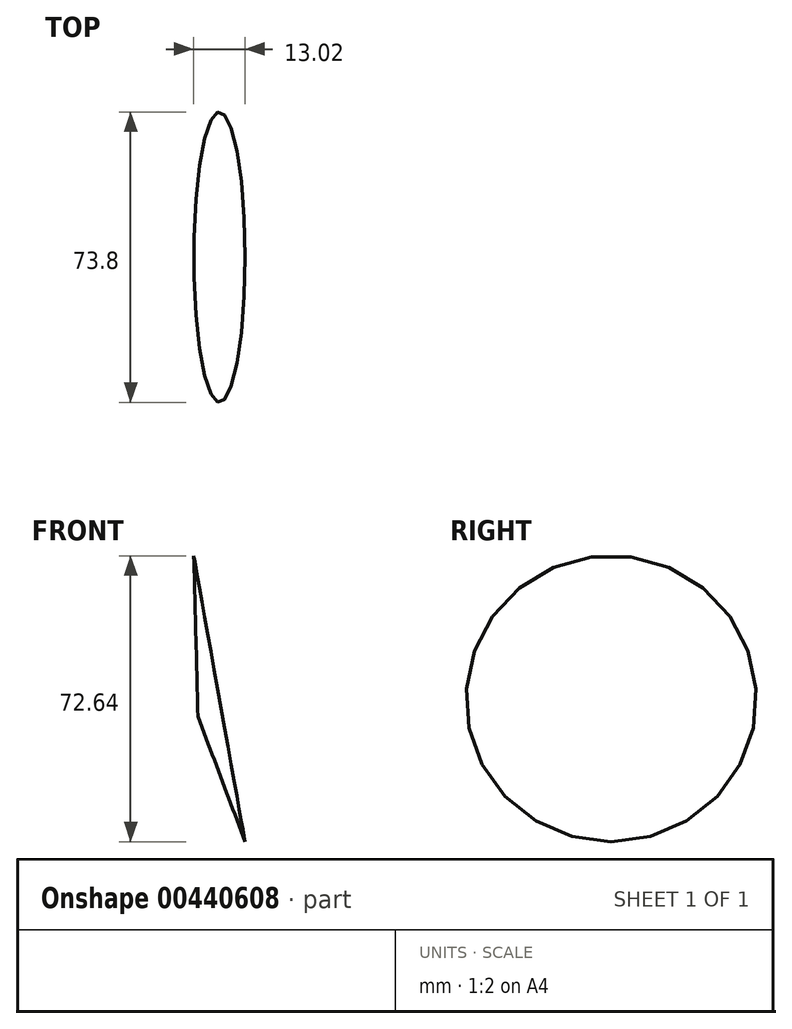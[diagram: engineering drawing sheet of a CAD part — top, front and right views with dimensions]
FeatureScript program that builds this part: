
annotation { "Feature Type Name" : "Feature", "Feature Type Description" : "" }
export const myFeature = defineFeature(function(context is Context, id is Id, definition is map)
    precondition{}
    {
        {
            var Q0;
            Q0=qCreatedBy(makeId("Front.planeOp"),FACE);
            var sketch = newSketch(context, id + "F0", { "sketchPlane" : qUnion([Q0])});
            skLineSegment(sketch, "E0", {"start": v(2.62, -61.14) * mm, "end": v(13.02, -91.95) * mm});
            skPoint(sketch, "E1.visualSharp", {"position": v(0, -53.36) * mm});
            skArc(sketch, "E1.filletArc", {"start": v(0, -45.15) * mm, "mid": v(0.66, -53.25) * mm, "end": v(2.62, -61.14) * mm});
            skLineSegment(sketch, "E2", {"start": v(0, -45.15) * mm, "end": v(0, -19.3) * mm});
            skLineSegment(sketch, "E3", {"start": v(0, -19.3) * mm, "end": v(13.02, -91.95) * mm, "construction": true});
            skPoint(sketch, "E4", {"position": v(6.05, -53.09) * mm});
            skPoint(sketch, "E5", {"position": v(1.05, -60.12) * mm});
            skPoint(sketch, "E6", {"position": v(5.07, -73.53) * mm});
            skPoint(sketch, "E7", {"position": v(6.35, -65.42) * mm});
            skPoint(sketch, "E8", {"position": v(1.05, -41.5) * mm});
            skPoint(sketch, "E9", {"position": v(-1.11, -36.28) * mm});
            skPoint(sketch, "E10", {"position": v(1.05, -29.22) * mm});
            skSolve(sketch);
        }
        {
            var Q0;
            Q0=sQuery(id+"F0.wireOp",EDGE,"E3");
            cPlane(context, id + "F1", {"entities" : qUnion([Q0]), "cplaneType" : CPlaneType.LINE_ANGLE, "offset" : 25 * mm, "angle" : 0 * degree, "width" : 150 * mm, "height" : 150 * mm});
        }
        {
            var Q0;
            Q0=qCreatedBy(id+"F1.planeOp",FACE);
            var sketch = newSketch(context, id + "F2", { "sketchPlane" : qUnion([Q0])});
            skLineSegment(sketch, "E11.0", {"start": v(0, -60.64) * mm, "end": v(0, -92.8) * mm, "construction": true});
            skLineSegment(sketch, "E12.0", {"start": v(0, -44.44) * mm, "end": v(0, -60.64) * mm, "construction": true});
            skLineSegment(sketch, "E13.0", {"start": v(0, -44.44) * mm, "end": v(0, -19) * mm, "construction": true});
            skSolve(sketch);
        }
        {
            var Q0;
            Q0=qCreatedBy(id+"F1.planeOp",FACE);
            var sketch = newSketch(context, id + "F3", { "sketchPlane" : qUnion([Q0])});
            skPoint(sketch, "E14.0", {"position": v(0, -19) * mm});
            skPoint(sketch, "E15.0", {"position": v(0, -92.8) * mm});
            skLineSegment(sketch, "E16", {"start": v(0, -19) * mm, "end": v(0, -92.8) * mm, "construction": true});
            skCircle(sketch, "E17", {"center": v(0, -55.9) * mm, "radius": 36.9 * mm});
            skSolve(sketch);
        }
        {
            var Q0;
            Q0=sQuery(id+"F0.wireOp",VERTEX,"E5");
            var Q1;
            Q1=makeQuery(id+"F3.imprint","IMPRINT",FACE,{"disambiguationData":[TD([[makeQuery(id+"F3.imprint","IMPRINT",EDGE,{"derivedFrom":sQuery(id+"F3.wireOp",EDGE,"E17")}),1.0]])]});
            loft(context, id + "F4", {"sheetProfilesArray" : [{ "sheetProfileEntities" : qUnion([Q0]) }, { "sheetProfileEntities" : qUnion([Q1]) }]});
        }
    });
